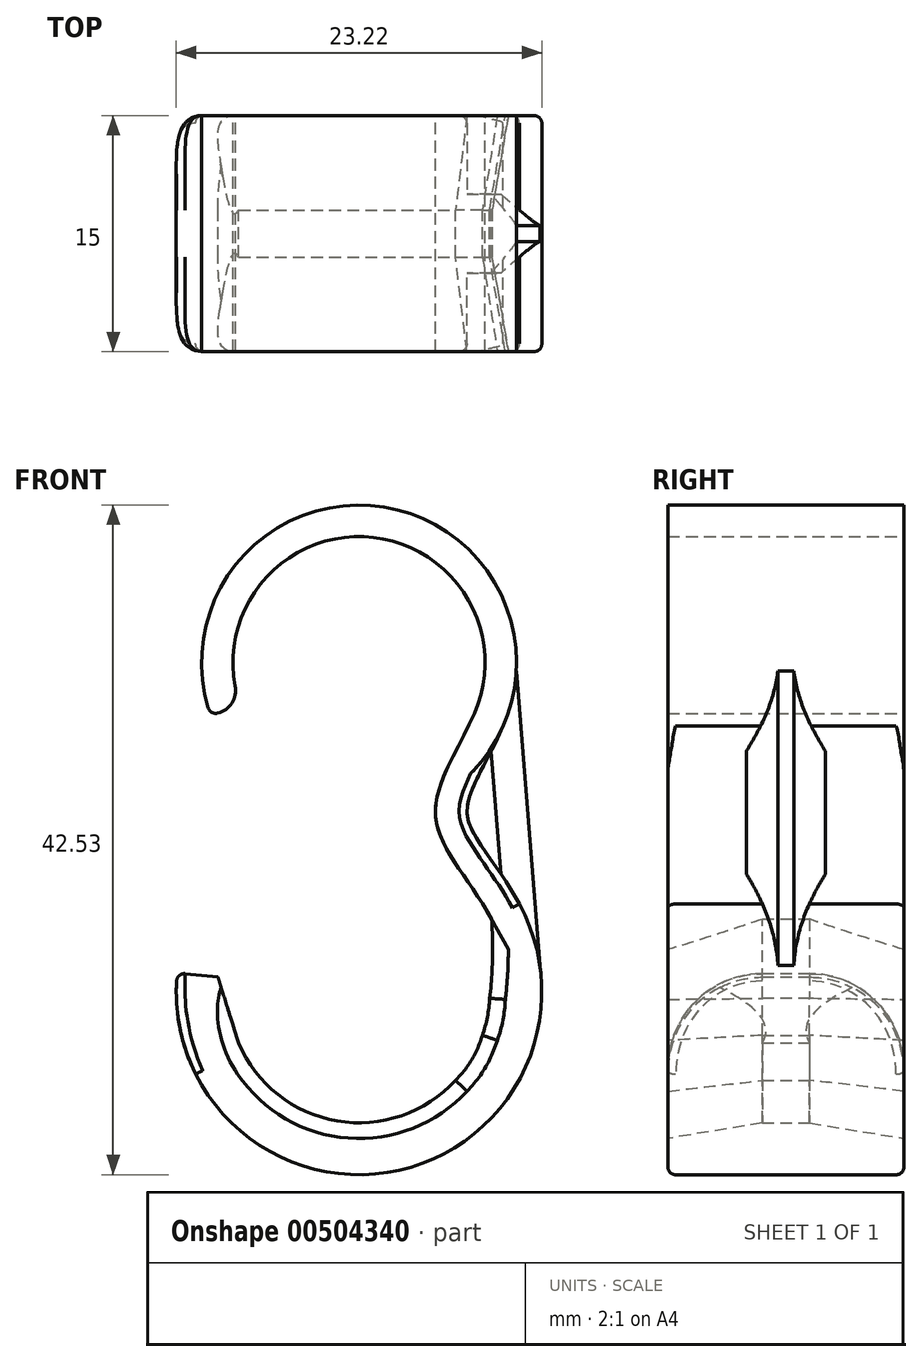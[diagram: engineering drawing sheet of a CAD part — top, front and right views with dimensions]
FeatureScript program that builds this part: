
annotation { "Feature Type Name" : "Feature", "Feature Type Description" : "" }
export const myFeature = defineFeature(function(context is Context, id is Id, definition is map)
    precondition{}
    {
        {
            var Q0;
            Q0=qCreatedBy(makeId("Front.planeOp"),FACE);
            var sketch = newSketch(context, id + "F0", { "sketchPlane" : qUnion([Q0])});
            skArc(sketch, "E0", {"start": v(7.32, 0) * mm, "mid": v(0, 11.23) * mm, "end": v(-7.32, 0) * mm});
            skArc(sketch, "E1", {"start": v(-9.55, -16.69) * mm, "mid": v(1.9, -27.11) * mm, "end": v(8.42, -13.07) * mm});
            skFitSpline(sketch, "E2", {"points": [v(7.32, 0) * mm, v(4.86, -6.52) * mm, v(8.42, -13.07) * mm], "startDerivative": vector(-6.34, -14.38) * mm, "endDerivative": vector(8.29, -15.1) * mm});
            skArc(sketch, "E3.0", {"start": v(9.15, -0.8) * mm, "mid": v(0.42, 13.22) * mm, "end": v(-9.45, -0.03) * mm});
            skFitSpline(sketch, "E3.1", {"points": [v(9.15, -0.8) * mm, v(8.86, -1.47) * mm, v(8.38, -2.4) * mm, v(7.8, -3.52) * mm, v(7.42, -4.3) * mm, v(7.13, -4.99) * mm, v(6.97, -5.49) * mm, v(6.9, -5.83) * mm, v(6.86, -6.05) * mm, v(6.85, -6.25) * mm, v(6.86, -6.41) * mm, v(6.89, -6.6) * mm, v(6.95, -6.86) * mm, v(7.11, -7.27) * mm, v(7.43, -7.87) * mm, v(7.86, -8.55) * mm, v(8.38, -9.31) * mm, v(9.16, -10.43) * mm, v(9.78, -11.4) * mm, v(10.17, -12.1) * mm]});
            skArc(sketch, "E3.2", {"start": v(-11.54, -16.48) * mm, "mid": v(2.3, -29.07) * mm, "end": v(10.17, -12.1) * mm});
            skLineSegment(sketch, "E4", {"start": v(-11.54, -16.48) * mm, "end": v(-9.55, -16.69) * mm});
            skLineSegment(sketch, "E5", {"start": v(-9.45, -0.03) * mm, "end": v(-7.32, 0) * mm});
            skLineSegment(sketch, "E6", {"start": v(9.99, 2.7) * mm, "end": v(11.48, -16) * mm});
            skArc(sketch, "E7.0", {"start": v(-8.26, -16.83) * mm, "mid": v(1.64, -25.84) * mm, "end": v(7.28, -13.7) * mm});
            skLineSegment(sketch, "E8", {"start": v(-9.55, -16.69) * mm, "end": v(-8.26, -16.83) * mm});
            skFitSpline(sketch, "E9", {"points": [v(6.13, -23.3) * mm, v(8.3, -18.08) * mm, v(8.42, -13.07) * mm], "startDerivative": vector(9.16, 9.08) * mm, "endDerivative": vector(-0.69, 10.38) * mm});
            skSolve(sketch);
        }
        {
            var Q0;
            Q0=makeQuery(id+"F0.imprint","IMPRINT",FACE,{"disambiguationData":[TD([[makeQuery(id+"F0.imprint","IMPRINT",EDGE,{"derivedFrom":sQuery(id+"F0.wireOp",EDGE,"E0")}),-1.0]])]});
            extrude(context, id + "F1", {"entities" : qUnion([Q0]), "endBound" : BoundingType.SYMMETRIC, "depth" : 15 * mm});
        }
        {
            var Q0;
            {var subQ6=sQuery(id+"F0.wireOp",EDGE,"E1");Q0=makeQuery(id+"F0.imprint","IMPRINT",FACE,{"disambiguationData":[TD([[makeQuery(id+"F0.imprint","IMPRINT",EDGE,{"derivedFrom":subQ6}),1.0]])]});}
            extrude(context, id + "F2", {"entities" : qUnion([Q0]), "operationType" : NewBodyOperationType.ADD, "endBound" : BoundingType.SYMMETRIC, "depth" : 15 * mm});
        }
        {
            var Q0;
            {var subQ0=sQuery(id+"F0.wireOp",EDGE,"E3.1");Q0=makeQuery(id+"F0.imprint","IMPRINT",FACE,{"disambiguationData":[TD([[makeQuery(id+"F0.imprint","IMPRINT",EDGE,{"derivedFrom":subQ0}),1.0]])]});}
            extrude(context, id + "F3", {"entities" : qUnion([Q0]), "operationType" : NewBodyOperationType.ADD, "endBound" : BoundingType.SYMMETRIC, "depth" : 5 * mm});
        }
        {
            var Q0;
            {var subQ0=sQuery(id+"F0.wireOp",EDGE,"E7.0");Q0=makeQuery(id+"F2.opExtrude","CAP_EDGE",EDGE,{"disambiguationData":[OSD([subQ0]),TDD([makeQuery(id+"F0.imprint","IMPRINT",EDGE,{"disambiguationData":[TD([[makeQuery(id+"F0.imprint","INTERSECT",VERTEX,{"derivedFrom":[subQ0,sQuery(id+"F0.wireOp",EDGE,"E8")]}),-1.0]])],"derivedFrom":subQ0})])],"isStart":false});}
            var Q1;
            {var subQ0=sQuery(id+"F0.wireOp",EDGE,"E9");var subQ1=sQuery(id+"F0.wireOp",EDGE,"E7.0");Q1=makeQuery(id+"F2.opExtrude","CAP_EDGE",EDGE,{"disambiguationData":[OSD([subQ0]),TDD([makeQuery(id+"F0.imprint","IMPRINT",EDGE,{"disambiguationData":[TD([[makeQuery(id+"F0.imprint","INTERSECT",VERTEX,{"disambiguationData":[OD(0.0)],"derivedFrom":[subQ1,subQ0]}),-1.0]])],"derivedFrom":subQ0})])],"isStart":false});}
            var Q2;
            {var subQ0=sQuery(id+"F0.wireOp",EDGE,"E9");var subQ1=sQuery(id+"F0.wireOp",EDGE,"E7.0");Q2=makeQuery(id+"F2.opExtrude","CAP_EDGE",EDGE,{"disambiguationData":[OSD([subQ1]),TDD([makeQuery(id+"F0.imprint","IMPRINT",EDGE,{"disambiguationData":[TD([[makeQuery(id+"F0.imprint","INTERSECT",VERTEX,{"disambiguationData":[OD(1.0)],"derivedFrom":[subQ1,subQ0]}),1.0]])],"derivedFrom":subQ1})])],"isStart":false});}
            var Q3;
            {var subQ0=sQuery(id+"F0.wireOp",EDGE,"E9");Q3=makeQuery(id+"F2.opExtrude","CAP_EDGE",EDGE,{"disambiguationData":[OSD([subQ0]),TDD([makeQuery(id+"F0.imprint","IMPRINT",EDGE,{"disambiguationData":[TD([[makeQuery(id+"F0.imprint","INTERSECT",VERTEX,{"disambiguationData":[OD(1.0)],"derivedFrom":[sQuery(id+"F0.wireOp",EDGE,"E7.0"),subQ0]}),-1.0]])],"derivedFrom":subQ0})])],"isStart":false});}
            var Q4;
            {var subQ0=sQuery(id+"F0.wireOp",EDGE,"E7.0");Q4=makeQuery(id+"F2.opExtrude","CAP_EDGE",EDGE,{"disambiguationData":[OSD([subQ0]),TDD([makeQuery(id+"F0.imprint","IMPRINT",EDGE,{"disambiguationData":[TD([[makeQuery(id+"F0.imprint","INTERSECT",VERTEX,{"derivedFrom":[subQ0,sQuery(id+"F0.wireOp",EDGE,"E8")]}),-1.0]])],"derivedFrom":subQ0})])],"isStart":true});}
            var Q5;
            {var subQ0=sQuery(id+"F0.wireOp",EDGE,"E9");var subQ1=sQuery(id+"F0.wireOp",EDGE,"E7.0");Q5=makeQuery(id+"F2.opExtrude","CAP_EDGE",EDGE,{"disambiguationData":[OSD([subQ0]),TDD([makeQuery(id+"F0.imprint","IMPRINT",EDGE,{"disambiguationData":[TD([[makeQuery(id+"F0.imprint","INTERSECT",VERTEX,{"disambiguationData":[OD(0.0)],"derivedFrom":[subQ1,subQ0]}),-1.0]])],"derivedFrom":subQ0})])],"isStart":true});}
            var Q6;
            {var subQ0=sQuery(id+"F0.wireOp",EDGE,"E9");var subQ1=sQuery(id+"F0.wireOp",EDGE,"E7.0");Q6=makeQuery(id+"F2.opExtrude","CAP_EDGE",EDGE,{"disambiguationData":[OSD([subQ1]),TDD([makeQuery(id+"F0.imprint","IMPRINT",EDGE,{"disambiguationData":[TD([[makeQuery(id+"F0.imprint","INTERSECT",VERTEX,{"disambiguationData":[OD(1.0)],"derivedFrom":[subQ1,subQ0]}),1.0]])],"derivedFrom":subQ1})])],"isStart":true});}
            var Q7;
            {var subQ0=sQuery(id+"F0.wireOp",EDGE,"E9");Q7=makeQuery(id+"F2.opExtrude","CAP_EDGE",EDGE,{"disambiguationData":[OSD([subQ0]),TDD([makeQuery(id+"F0.imprint","IMPRINT",EDGE,{"disambiguationData":[TD([[makeQuery(id+"F0.imprint","INTERSECT",VERTEX,{"disambiguationData":[OD(1.0)],"derivedFrom":[sQuery(id+"F0.wireOp",EDGE,"E7.0"),subQ0]}),-1.0]])],"derivedFrom":subQ0})])],"isStart":true});}
            chamfer(context, id + "F4", {"entities" : qUnion([Q0, Q1, Q2, Q3, Q4, Q5, Q6, Q7]), "chamferType" : ChamferType.TWO_OFFSETS, "width1" : 6 * mm, "oppositeDirection" : false, "width2" : 1 * mm, "tangentPropagation" : true});
        }
        {
            var Q0;
            Q0=makeQuery(id+"F1.opExtrude","SWEPT_EDGE",EDGE,{"disambiguationData":[OSD([sQuery(id+"F0.wireOp",EDGE,"E3.2"),sQuery(id+"F0.wireOp",EDGE,"E4")])]});
            var Q1;
            Q1=makeQuery(id+"F1.opExtrude","CAP_EDGE",EDGE,{"disambiguationData":[OSD([sQuery(id+"F0.wireOp",EDGE,"E3.2")])],"isStart":false});
            var Q2;
            Q2=makeQuery(id+"F1.opExtrude","CAP_EDGE",EDGE,{"disambiguationData":[OSD([sQuery(id+"F0.wireOp",EDGE,"E3.2")])],"isStart":true});
            fillet(context, id + "F5", {"entities" : qUnion([Q0, Q1, Q2]), "radius" : 0.5 * mm, "tangentPropagation" : true, "allowEdgeOverflow" : false});
        }
        {
            var Q0;
            Q0=makeQuery(id+"F1.opExtrude","SWEPT_EDGE",EDGE,{"disambiguationData":[OSD([sQuery(id+"F0.wireOp",EDGE,"E0"),sQuery(id+"F0.wireOp",EDGE,"E5")])]});
            fillet(context, id + "F6", {"entities" : qUnion([Q0]), "radius" : 1.5 * mm, "tangentPropagation" : true, "allowEdgeOverflow" : false});
        }
        {
            var Q0;
            Q0=makeQuery(id+"F1.opExtrude","SWEPT_EDGE",EDGE,{"disambiguationData":[OSD([sQuery(id+"F0.wireOp",EDGE,"E3.0"),sQuery(id+"F0.wireOp",EDGE,"E5")])]});
            fillet(context, id + "F7", {"entities" : qUnion([Q0]), "radius" : 0.5 * mm, "tangentPropagation" : true, "allowEdgeOverflow" : false});
        }
        {
            var Q0;
            Q0=makeQuery(id+"F2.boolean.opBoolean","MERGE",EDGE,{"derivedFrom":[makeQuery(id+"F1.opExtrude","CAP_EDGE",EDGE,{"disambiguationData":[OSD([sQuery(id+"F0.wireOp",EDGE,"E4")])],"isStart":false}),makeQuery(id+"F2.opExtrude","CAP_EDGE",EDGE,{"disambiguationData":[OSD([sQuery(id+"F0.wireOp",EDGE,"E8")])],"isStart":false})]});
            var Q1;
            Q1=makeQuery(id+"F2.boolean.opBoolean","MERGE",EDGE,{"derivedFrom":[makeQuery(id+"F1.opExtrude","CAP_EDGE",EDGE,{"disambiguationData":[OSD([sQuery(id+"F0.wireOp",EDGE,"E4")])],"isStart":true}),makeQuery(id+"F2.opExtrude","CAP_EDGE",EDGE,{"disambiguationData":[OSD([sQuery(id+"F0.wireOp",EDGE,"E8")])],"isStart":true})]});
            fillet(context, id + "F8", {"entities" : qUnion([Q0, Q1]), "radius" : 6 * mm, "tangentPropagation" : true, "allowEdgeOverflow" : false});
        }
        {
            var Q0;
            Q0=makeQuery(id+"F2.opExtrude","SWEPT_EDGE",EDGE,{"disambiguationData":[OSD([sQuery(id+"F0.wireOp",EDGE,"E7.0"),sQuery(id+"F0.wireOp",EDGE,"E8")])]});
            chamfer(context, id + "F9", {"entities" : qUnion([Q0]), "chamferType" : ChamferType.TWO_OFFSETS, "width1" : 2 * mm, "oppositeDirection" : false, "width2" : 5 * mm, "tangentPropagation" : true});
        }
        {
            var Q0;
            Q0=makeQuery(id+"F3.opExtrude","CAP_EDGE",EDGE,{"disambiguationData":[OSD([sQuery(id+"F0.wireOp",EDGE,"E6")])],"isStart":false});
            var Q1;
            Q1=makeQuery(id+"F3.opExtrude","CAP_EDGE",EDGE,{"disambiguationData":[OSD([sQuery(id+"F0.wireOp",EDGE,"E6")])],"isStart":true});
            chamfer(context, id + "F10", {"entities" : qUnion([Q0, Q1]), "width" : 2 * mm, "tangentPropagation" : true});
        }
    });
